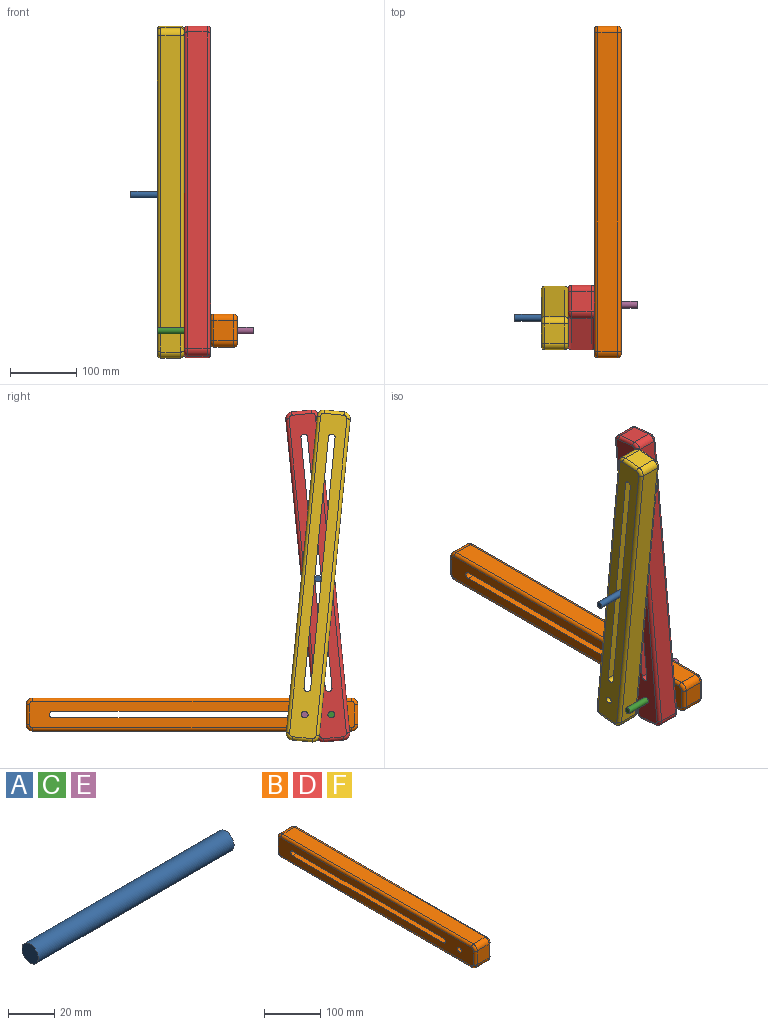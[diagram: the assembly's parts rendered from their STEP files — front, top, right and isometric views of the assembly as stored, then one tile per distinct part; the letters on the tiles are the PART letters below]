
ASSEMBLY  parts=6 mates=7
PART A: 3 faces, bbox 120x10x10 mm
  f0: cylinder r=5mm len=120mm, axis (1,0,0), area 3769.9mm2, adj f1,f2
  f1: plane 10x10mm, normal (-1,0,0), area 78.5mm2, adj f0
  f2: plane 10x10mm, normal (1,0,0), area 78.5mm2, adj f0
PART B: 31 faces, bbox 40x501.6x51.6 mm
  f0: plane 380x40mm, normal (0,0,-1), area 15200mm2, adj f1,f8,f9,f10
  f1: cylinder r=5mm len=40mm, axis (1,0,0), area 628.3mm2, adj f0,f2,f9,f10
  f2: plane 380x40mm, normal (0,0,1), area 15200mm2, adj f1,f8,f9,f10
  f3: plane 480x30mm, normal (0,0,-1), area 14400mm2, adj f11,f14,f22,f30
  f4: plane 30x30mm, normal (0,1,0), area 900mm2, adj f11,f12,f18,f26
  f5: plane 480x30mm, normal (0,0,1), area 14400mm2, adj f12,f13,f15,f23
  f6: plane 30x30mm, normal (0,-1,0), area 900mm2, adj f13,f14,f19,f27
  f7: cylinder r=5mm len=40mm, axis (1,0,0), area 1256.6mm2, adj f9,f10
  f8: cylinder r=5mm len=40mm, axis (1,0,0), area 628.3mm2, adj f0,f2,f9,f10
  f9: plane 490x40mm, normal (-1,0,0), area 15621.5mm2, adj f0,f1,f2,f7,f8,f15,f16,f17
  f10: plane 490x40mm, normal (1,0,0), area 15621.5mm2, adj f0,f1,f2,f7,f8,f23,f24,f25
  f11: cylinder r=10mm len=30mm, axis (1,0,0), area 471.2mm2, adj f3,f4,f20,f28
  f12: cylinder r=10mm len=30mm, axis (-1,0,0), area 471.2mm2, adj f4,f5,f16,f24
  f13: cylinder r=10mm len=30mm, axis (1,0,0), area 471.2mm2, adj f5,f6,f17,f25
  f14: cylinder r=10mm len=30mm, axis (-1,0,0), area 471.2mm2, adj f3,f6,f21,f29
  f15: cylinder r=5mm len=480mm, axis (0,1,0), area 3769.9mm2, adj f5,f9,f16,f17
  f16: torus R=5mm, axis (1,0,0), area 101mm2, adj f9,f12,f15,f18
  f17: torus R=5mm, axis (1,0,0), area 101mm2, adj f9,f13,f15,f19
  f18: cylinder r=5mm len=30mm, axis (0,0,-1), area 235.6mm2, adj f4,f9,f16,f20
  f19: cylinder r=5mm len=30mm, axis (0,0,1), area 235.6mm2, adj f6,f9,f17,f21
  f20: torus R=5mm, axis (1,0,0), area 101mm2, adj f9,f11,f18,f22
  f21: torus R=5mm, axis (1,0,0), area 101mm2, adj f9,f14,f19,f22
  f22: cylinder r=5mm len=480mm, axis (0,-1,0), area 3769.9mm2, adj f3,f9,f20,f21
  f23: cylinder r=5mm len=480mm, axis (0,-1,0), area 3769.9mm2, adj f5,f10,f24,f25
  f24: torus R=5mm, axis (1,0,0), area 101mm2, adj f10,f12,f23,f26
  f25: torus R=5mm, axis (1,0,0), area 101mm2, adj f10,f13,f23,f27
  f26: cylinder r=5mm len=30mm, axis (0,0,1), area 235.6mm2, adj f4,f10,f24,f28
  f27: cylinder r=5mm len=30mm, axis (0,0,-1), area 235.6mm2, adj f6,f10,f25,f29
  f28: torus R=5mm, axis (1,0,0), area 101mm2, adj f10,f11,f26,f30
  f29: torus R=5mm, axis (1,0,0), area 101mm2, adj f10,f14,f27,f30
  f30: cylinder r=5mm len=480mm, axis (0,1,0), area 3769.9mm2, adj f3,f10,f28,f29
PART C: same geometry as A
PART D: same geometry as B
PART E: same geometry as A
PART F: same geometry as B
PLACE A rot(axis=(1,0,0),48.6deg) t=(-82.01,-68.06,-52.73)mm
PLACE B t=(-42.01,122.17,-257.59)mm fixed
PLACE C t=(-42.01,-88.18,-257.59)mm
PLACE D rot(axis=(1,0,0),84.4deg) t=(-82.01,-67.45,-48.58)mm
PLACE E rot(axis=(-1,0,0),51.2deg) t=(-17.9,-48.05,-257.31)mm
PLACE F rot(axis=(1,0,0),95.6deg) t=(-122.01,-68.21,-48.58)mm
MATE cylindrical F.f10 <-> D.f9  axis (1,0,0) through (-122.01,-67.83,-52.47)mm
MATE cylindrical A.f0 <-> D.f10  axis (1,0,0) through (-82.01,-67.83,-52.47)mm
MATE planar F.f10 <-> D.f9  axis (1,0,0) through (-122.01,-67.83,-52.47)mm
MATE cylindrical E.f0 <-> F.f7  axis (1,0,0) through (-137.9,-47.83,-257.59)mm
MATE planar D.f10 <-> B.f9  axis (1,0,0) through (-82.01,-67.83,-52.47)mm
MATE cylindrical C.f0 <-> B.f7  axis (1,0,0) through (-42.01,-87.83,-257.59)mm
MATE cylindrical D.f7 <-> B.f7  axis (1,0,0) through (-82.01,-87.83,-257.59)mm
